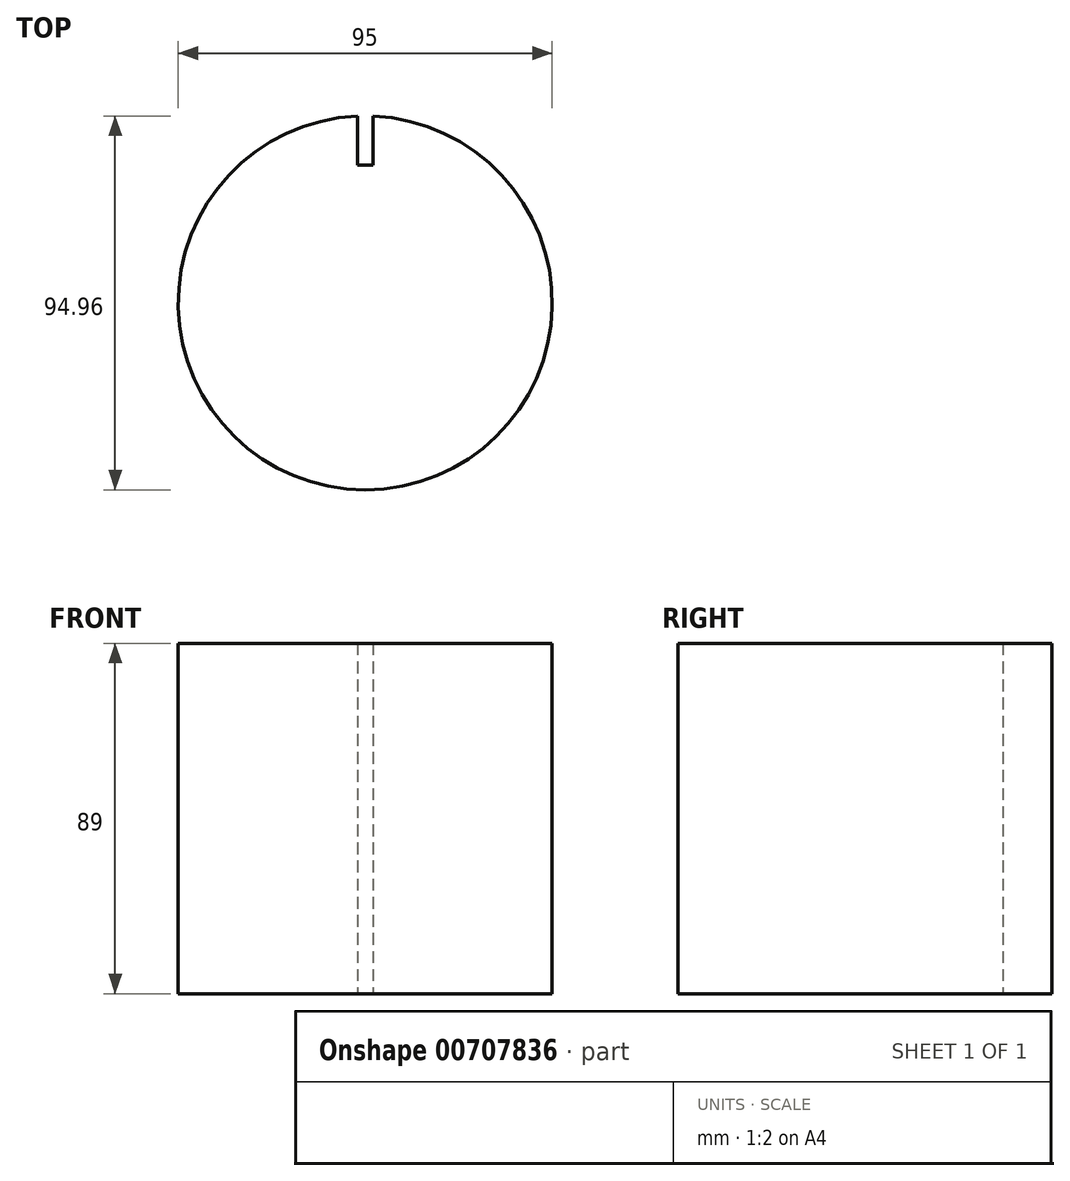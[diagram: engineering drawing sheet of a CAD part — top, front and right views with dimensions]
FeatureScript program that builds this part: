
annotation { "Feature Type Name" : "Feature", "Feature Type Description" : "" }
export const myFeature = defineFeature(function(context is Context, id is Id, definition is map)
    precondition{}
    {
        {
            var Q0;
            Q0=qCreatedBy(makeId("Top.planeOp"),FACE);
            var sketch = newSketch(context, id + "F0", { "sketchPlane" : qUnion([Q0])});
            skCircle(sketch, "E0", {"center": v(0, 0) * mm, "radius": 47.5 * mm});
            skLineSegment(sketch, "E1", {"start": v(0, 0) * mm, "end": v(0, 47.5) * mm});
            skLineSegment(sketch, "E2.bottom", {"start": v(2, 34.97) * mm, "end": v(-2, 34.97) * mm});
            skLineSegment(sketch, "E2.top", {"start": v(2, 60.03) * mm, "end": v(-2, 60.03) * mm});
            skLineSegment(sketch, "E2.left", {"start": v(2, 34.97) * mm, "end": v(2, 60.03) * mm});
            skLineSegment(sketch, "E2.right", {"start": v(-2, 34.97) * mm, "end": v(-2, 60.03) * mm});
            skPoint(sketch, "E2.middle", {"position": v(0, 47.5) * mm});
            skSolve(sketch);
        }
        {
            var Q0;
            {var subQ4=sQuery(id+"F0.wireOp",EDGE,"E2.left");var subQ6=sQuery(id+"F0.wireOp",EDGE,"E0");var subQ7=makeQuery(id+"F0.imprint","INTERSECT",VERTEX,{"derivedFrom":[subQ6,subQ4]});Q0=makeQuery(id+"F0.imprint","IMPRINT",FACE,{"disambiguationData":[TD([[makeQuery(id+"F0.imprint","IMPRINT",EDGE,{"disambiguationData":[TD([[subQ7,1.0]])],"derivedFrom":subQ6}),1.0]])]});}
            extrude(context, id + "F1", {"entities" : qUnion([Q0]), "depth" : 89 * mm, "offsetDistance" : 25 * mm});
        }
    });
